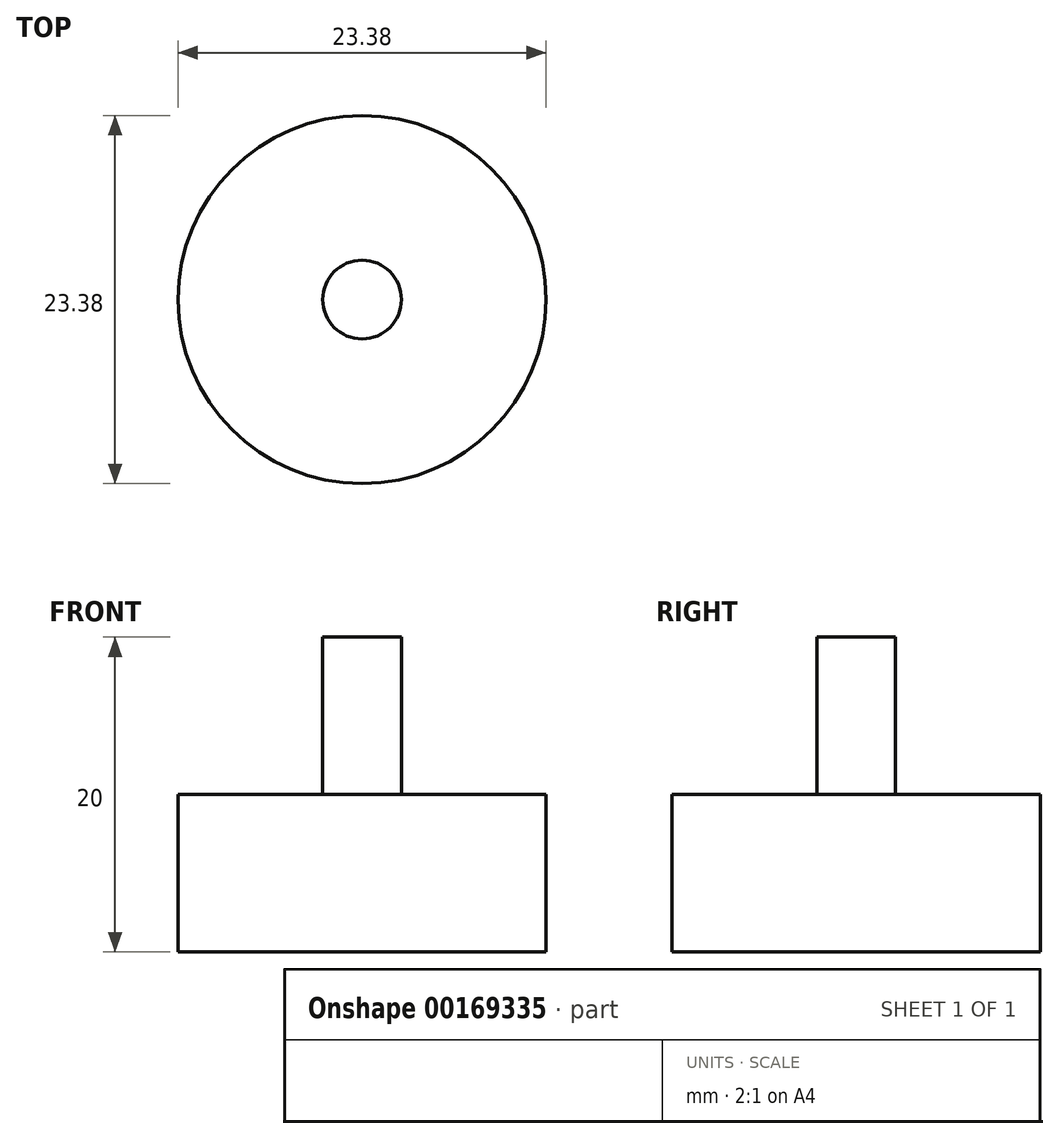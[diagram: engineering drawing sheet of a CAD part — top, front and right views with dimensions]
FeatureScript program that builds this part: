
annotation { "Feature Type Name" : "Feature", "Feature Type Description" : "" }
export const myFeature = defineFeature(function(context is Context, id is Id, definition is map)
    precondition{}
    {
        {
            var Q0;
            Q0=qCreatedBy(makeId("Front.planeOp"),FACE);
            var sketch = newSketch(context, id + "F0", { "sketchPlane" : qUnion([Q0])});
            skLineSegment(sketch, "E0.bottom", {"start": v(0, 0) * mm, "end": v(2.5, 0) * mm});
            skLineSegment(sketch, "E0.top", {"start": v(0, 10) * mm, "end": v(2.5, 10) * mm});
            skLineSegment(sketch, "E0.left", {"start": v(0, 0) * mm, "end": v(0, 10) * mm});
            skLineSegment(sketch, "E0.right", {"start": v(2.5, 0) * mm, "end": v(2.5, 10) * mm});
            skLineSegment(sketch, "E1.bottom", {"start": v(0, 0) * mm, "end": v(11.69, 0) * mm});
            skLineSegment(sketch, "E1.top", {"start": v(0, -10) * mm, "end": v(11.69, -10) * mm});
            skLineSegment(sketch, "E1.left", {"start": v(0, 0) * mm, "end": v(0, -10) * mm});
            skLineSegment(sketch, "E1.right", {"start": v(11.69, 0) * mm, "end": v(11.69, -10) * mm});
            skLineSegment(sketch, "E2.bottom", {"start": v(0, -10) * mm, "end": v(2.5, -10) * mm});
            skLineSegment(sketch, "E2.top", {"start": v(0, -80) * mm, "end": v(2.5, -80) * mm});
            skLineSegment(sketch, "E2.left", {"start": v(0, -10) * mm, "end": v(0, -80) * mm});
            skLineSegment(sketch, "E2.right", {"start": v(2.5, -10) * mm, "end": v(2.5, -80) * mm});
            skSolve(sketch);
        }
        {
            var Q0;
            Q0=makeQuery(id+"F0.imprint","IMPRINT",FACE,{"disambiguationData":[TD([[makeQuery(id+"F0.imprint","IMPRINT",EDGE,{"derivedFrom":sQuery(id+"F0.wireOp",EDGE,"E1.top")}),1.0]])]});
            var Q1;
            Q1=makeQuery(id+"F0.imprint","IMPRINT",FACE,{"disambiguationData":[TD([[makeQuery(id+"F0.imprint","IMPRINT",EDGE,{"derivedFrom":sQuery(id+"F0.wireOp",EDGE,"E0.top")}),-1.0]])]});
            var Q2;
            Q2=makeQuery(id+"F0.imprint","IMPRINT",FACE,{"disambiguationData":[TD([[makeQuery(id+"F0.imprint","IMPRINT",EDGE,{"derivedFrom":sQuery(id+"F0.wireOp",EDGE,"E2.bottom")}),-1.0]])]});
            var Q3;
            Q3=sQuery(id+"F0.wireOp",EDGE,"E2.left");
            revolve(context, id + "F1", {"entities" : qUnion([Q0, Q1, Q2]), "axis" : qUnion([Q3]), "revolveType" : RevolveType.FULL});
        }
    });
